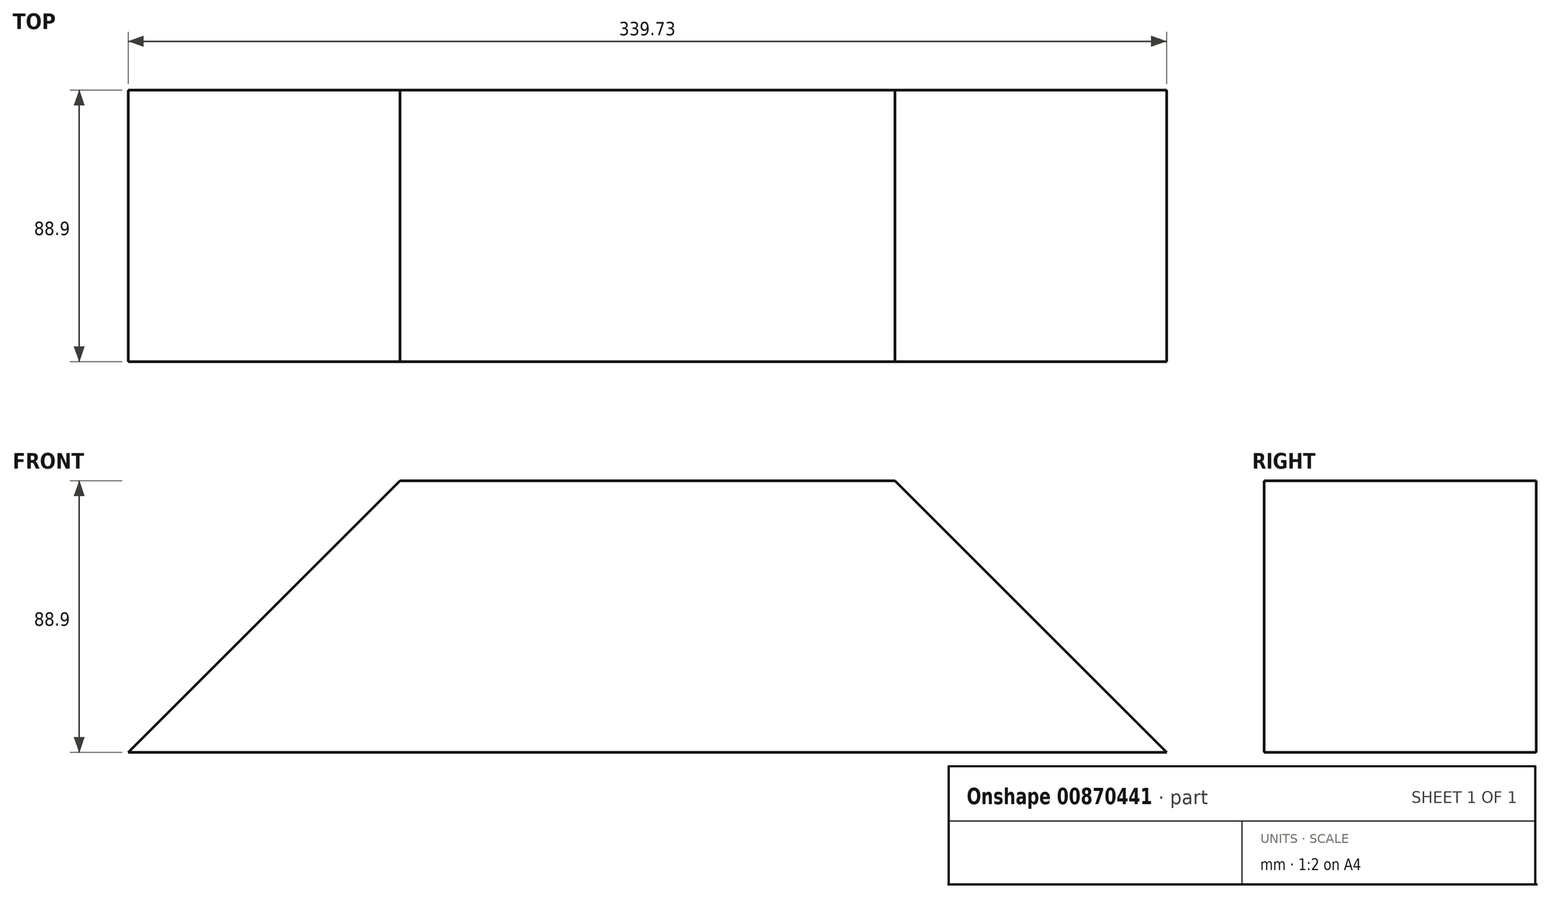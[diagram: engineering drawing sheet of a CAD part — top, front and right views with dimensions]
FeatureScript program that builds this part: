
annotation { "Feature Type Name" : "Feature", "Feature Type Description" : "" }
export const myFeature = defineFeature(function(context is Context, id is Id, definition is map)
    precondition{}
    {
        {
            var Q0;
            Q0=qCreatedBy(makeId("Right.planeOp"),FACE);
            var sketch = newSketch(context, id + "F0", { "sketchPlane" : qUnion([Q0])});
            skLineSegment(sketch, "E0.bottom", {"start": v(46.26, 44.45) * mm, "end": v(-42.64, 44.45) * mm});
            skLineSegment(sketch, "E0.top", {"start": v(46.26, -44.45) * mm, "end": v(-42.64, -44.45) * mm});
            skLineSegment(sketch, "E0.left", {"start": v(46.26, 44.45) * mm, "end": v(46.26, -44.45) * mm});
            skLineSegment(sketch, "E0.right", {"start": v(-42.64, 44.45) * mm, "end": v(-42.64, -44.45) * mm});
            skPoint(sketch, "E0.middle", {"position": v(1.8, 0) * mm});
            skSolve(sketch);
        }
        {
            var Q0;
            Q0=makeQuery(id+"F0.imprint","IMPRINT",FACE,{"disambiguationData":[TD([[makeQuery(id+"F0.imprint","IMPRINT",EDGE,{"derivedFrom":sQuery(id+"F0.wireOp",EDGE,"E0.bottom")}),1.0]])]});
            extrude(context, id + "F1", {"entities" : qUnion([Q0]), "depth" : 339.72 * mm, "offsetDistance" : 25.4 * mm});
        }
        {
            var Q0;
            Q0=makeQuery(id+"F1.opExtrude","SWEPT_FACE",FACE,{"disambiguationData":[OSD([sQuery(id+"F0.wireOp",EDGE,"E0.right")])]});
            var sketch = newSketch(context, id + "F2", { "sketchPlane" : qUnion([Q0])});
            skLineSegment(sketch, "E1", {"start": v(0, -44.45) * mm, "end": v(88.9, 44.45) * mm});
            skLineSegment(sketch, "E2", {"start": v(88.9, 44.45) * mm, "end": v(0, 44.45) * mm});
            skLineSegment(sketch, "E3", {"start": v(0, 44.45) * mm, "end": v(0, -44.45) * mm});
            skSolve(sketch);
        }
        {
            var Q0;
            Q0=makeQuery(id+"F2.imprint","IMPRINT",FACE,{"disambiguationData":[TD([[makeQuery(id+"F2.imprint","IMPRINT",EDGE,{"derivedFrom":sQuery(id+"F2.wireOp",EDGE,"E1")}),1.0]])]});
            extrude(context, id + "F3", {"entities" : qUnion([Q0]), "operationType" : NewBodyOperationType.REMOVE, "endBound" : BoundingType.THROUGH_ALL, "oppositeDirection" : true, "depth" : 25.4 * mm, "offsetDistance" : 25.4 * mm});
        }
        {
            var Q0;
            Q0=makeQuery(id+"F1.opExtrude","SWEPT_FACE",FACE,{"disambiguationData":[OSD([sQuery(id+"F0.wireOp",EDGE,"E0.right")])]});
            var sketch = newSketch(context, id + "F4", { "sketchPlane" : qUnion([Q0])});
            skLineSegment(sketch, "E4", {"start": v(339.73, -44.45) * mm, "end": v(250.83, 44.45) * mm});
            skLineSegment(sketch, "E5", {"start": v(250.83, 44.45) * mm, "end": v(339.73, 44.45) * mm});
            skLineSegment(sketch, "E6", {"start": v(339.73, 44.45) * mm, "end": v(339.73, -44.45) * mm});
            skSolve(sketch);
        }
        {
            var Q0;
            Q0=makeQuery(id+"F4.imprint","IMPRINT",FACE,{"disambiguationData":[TD([[makeQuery(id+"F4.imprint","IMPRINT",EDGE,{"derivedFrom":sQuery(id+"F4.wireOp",EDGE,"E4")}),-1.0]])]});
            extrude(context, id + "F5", {"entities" : qUnion([Q0]), "operationType" : NewBodyOperationType.REMOVE, "endBound" : BoundingType.THROUGH_ALL, "oppositeDirection" : true, "depth" : 25.4 * mm, "offsetDistance" : 25.4 * mm});
        }
    });
